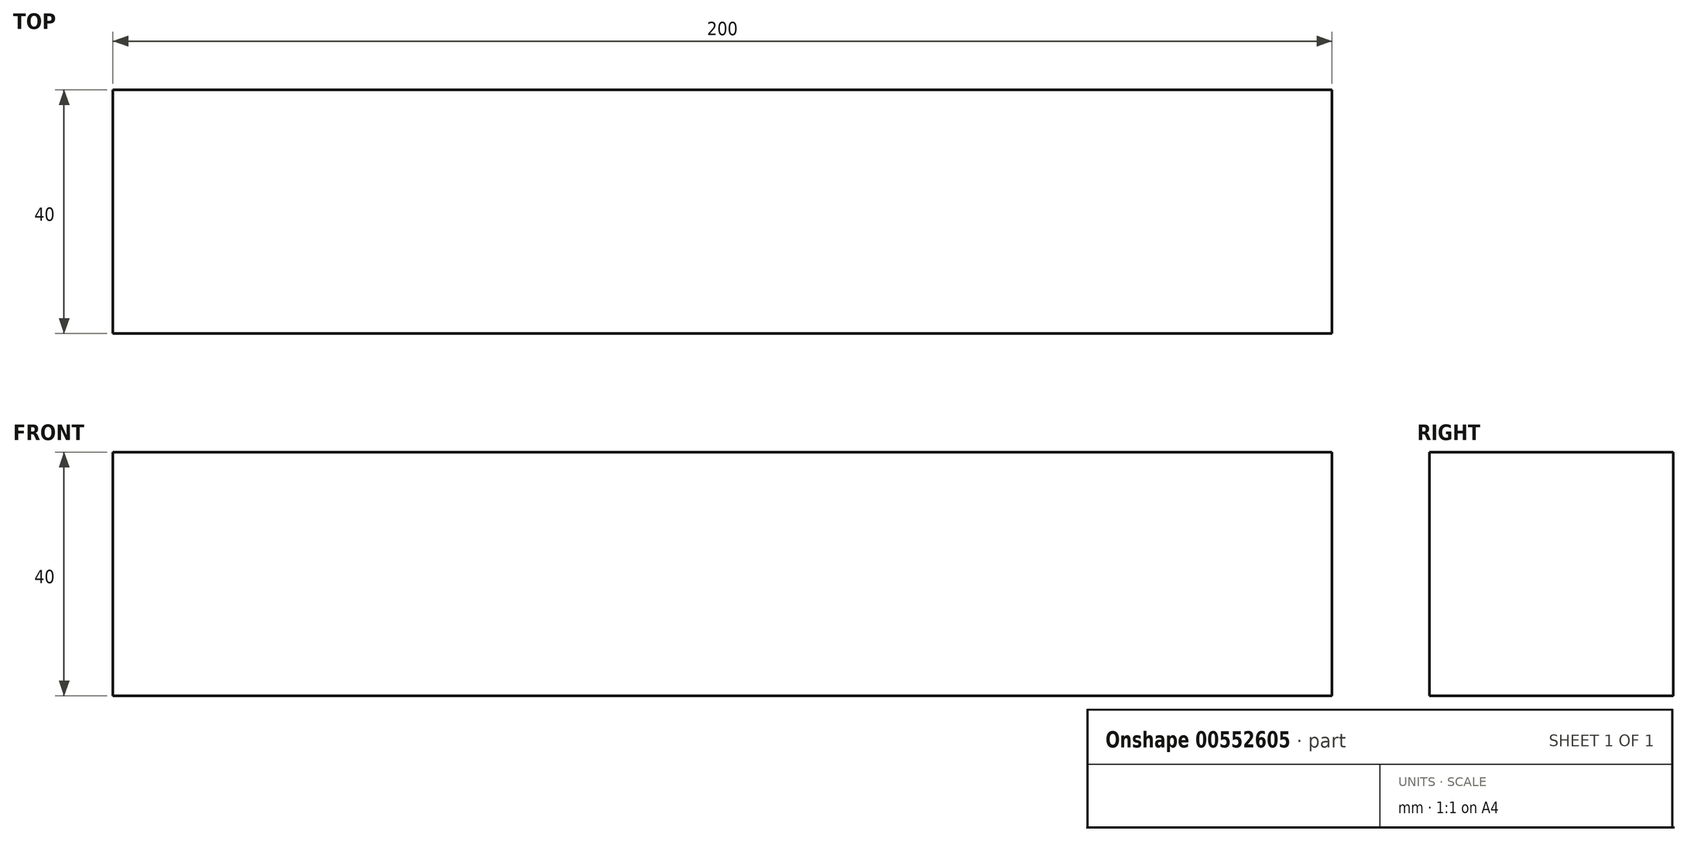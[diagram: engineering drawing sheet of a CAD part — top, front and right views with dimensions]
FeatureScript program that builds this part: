
annotation { "Feature Type Name" : "Feature", "Feature Type Description" : "" }
export const myFeature = defineFeature(function(context is Context, id is Id, definition is map)
    precondition{}
    {
        {
            var Q0;
            Q0=qCreatedBy(makeId("Front.planeOp"),FACE);
            var sketch = newSketch(context, id + "F0", { "sketchPlane" : qUnion([Q0])});
            skLineSegment(sketch, "E0.bottom", {"start": v(-100, 20) * mm, "end": v(100, 20) * mm});
            skLineSegment(sketch, "E0.top", {"start": v(-100, -20) * mm, "end": v(100, -20) * mm});
            skLineSegment(sketch, "E0.left", {"start": v(-100, 20) * mm, "end": v(-100, -20) * mm});
            skLineSegment(sketch, "E0.right", {"start": v(100, 20) * mm, "end": v(100, -20) * mm});
            skPoint(sketch, "E0.middle", {"position": v(0, 0) * mm});
            skSolve(sketch);
        }
        {
            var Q0;
            Q0 = qSketchRegion(id + "F0", true);
            extrude(context, id + "F1", {"entities" : qUnion([Q0]), "depth" : 40 * mm, "offsetDistance" : 25 * mm});
        }
    });
